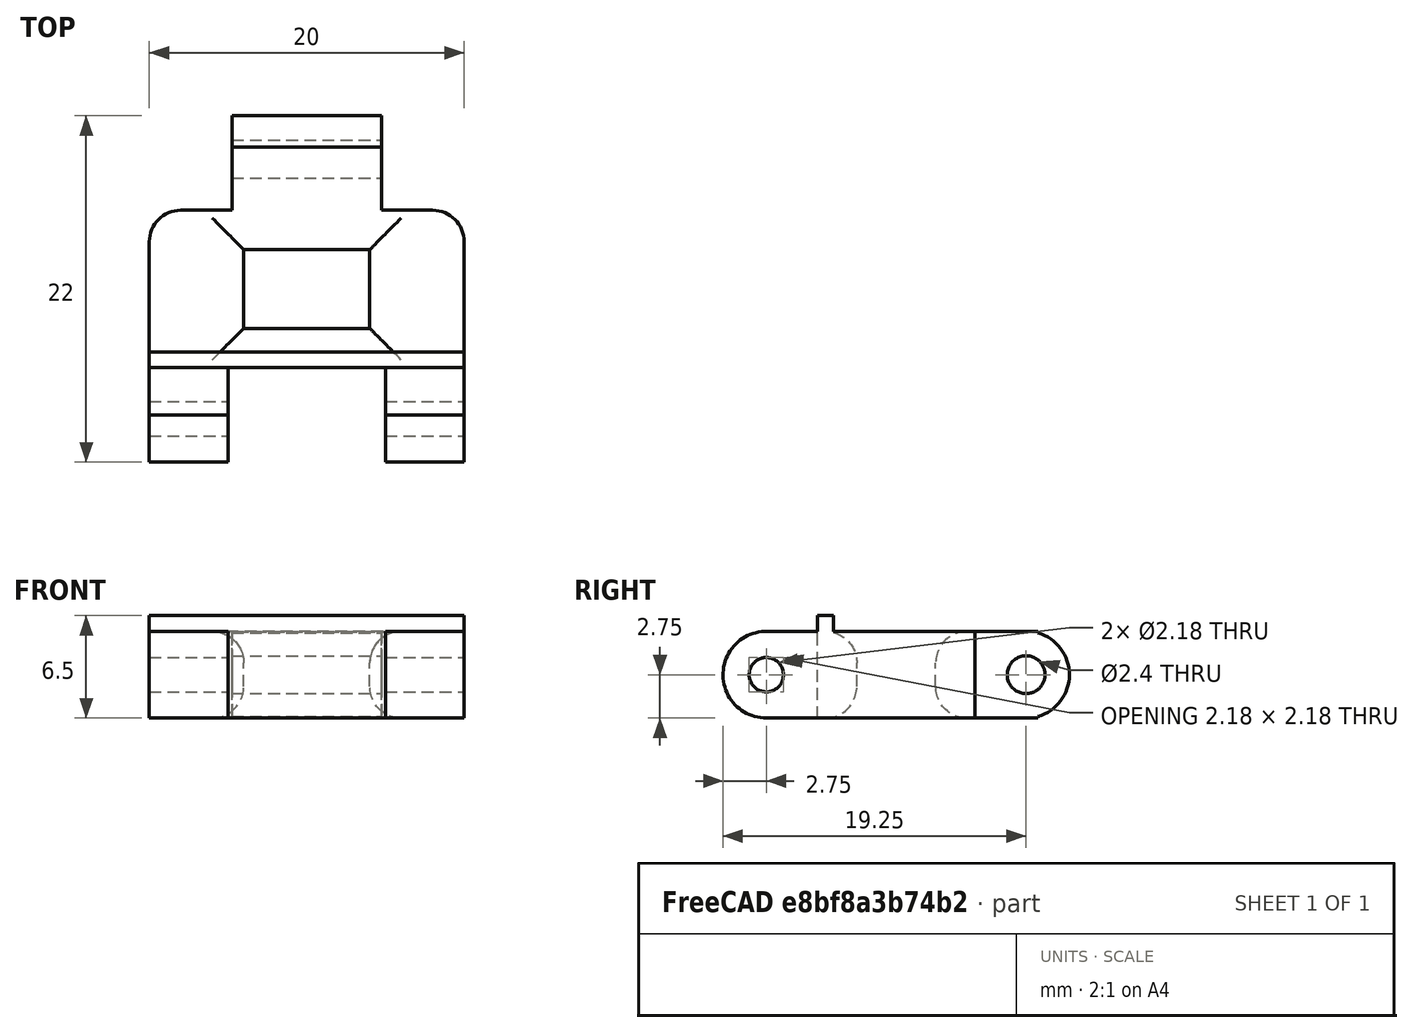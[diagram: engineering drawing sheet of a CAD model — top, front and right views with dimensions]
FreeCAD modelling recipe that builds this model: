
FCSTD DOCUMENT
Label: TankTread1.0
objects: Part::Box×5, Part::Cylinder×4, Part::Cut×4, Part::MultiFuse×2, Part::Fillet×2, Mesh::Feature×1
note: 17 computed .brp shape members not serialized (recipe doc carries the construction recipe); baked Part::Feature solids carry a one-line shape summary decoded from their .brp

FEATURE [Mesh::Feature] tanklink
FEATURE [Part::Cylinder] Cylinder
  Angle = 360
  Height = 20
  Placement = pos=(-1,1.75,2.75) rot=(0,1,0;1.5708rad)
  Radius = 2.75
FEATURE [Part::Box] Box
  Height = 5.5
  Length = 20
  Placement = pos=(-1,2,0) rot=(0,0,1;0rad)
  Width = 13
FEATURE [Part::Cylinder] Cylinder001
  Angle = 360
  Height = 9.5
  Placement = pos=(4.25,18.25,2.75) rot=(0,1,0;1.5708rad)
  Radius = 2.75
FEATURE [Part::Box] Box001
  Height = 5.5
  Length = 9.5
  Placement = pos=(4.25,15,0) rot=(0,0,1;0rad)
  Width = 4
FEATURE [Part::Box] Box002
  Height = 10
  Length = 8
  Placement = pos=(5,7.5,-2) rot=(0,0,1;0rad)
  Width = 5
FEATURE [Part::MultiFuse] Fusion
  Shapes = -> [Cylinder,Box,Box001,Cylinder001]
FEATURE [Part::Cut] Cut
  Base = -> Fusion
  Tool = -> Box002
FEATURE [Part::Fillet] Fillet
  Base = -> Cut
  Edges = 2 edges r=2: [Edge5,Edge32]
FEATURE [Part::Fillet] Fillet001
  Base = -> Fillet
  Edges = 8 edges r=2: [Edge14,Edge15,Edge16,Edge17,Edge28,Edge29,Edge30,Edge31]
FEATURE [Part::Box] Box003
  Height = 7
  Length = 10
  Placement = pos=(4,-2,-1) rot=(0,0,1;0rad)
  Width = 7
FEATURE [Part::Cut] Cut001
  Base = -> Fillet001
  Tool = -> Box003
FEATURE [Part::Cylinder] Cylinder002
  Angle = 360
  Height = 20
  Placement = pos=(-1,1.75,2.75) rot=(0,1,0;1.5708rad)
  Radius = 1.09
FEATURE [Part::Cylinder] Cylinder001001
  Angle = 360
  Height = 9.5
  Placement = pos=(4.25,18.25,2.75) rot=(0,1,0;1.5708rad)
  Radius = 1.2
FEATURE [Part::Cut] Cut002
  Base = -> Cut001
  Tool = -> Cylinder002
FEATURE [Part::Cut] Cut003
  Base = -> Cut002
  Tool = -> Cylinder001001
FEATURE [Part::Box] Box004
  Height = 1.5
  Length = 20
  Placement = pos=(-1,5,5) rot=(0,0,1;0rad)
  Width = 1
FEATURE [Part::MultiFuse] Fusion001
  Shapes = -> [Cut003,Box004]
